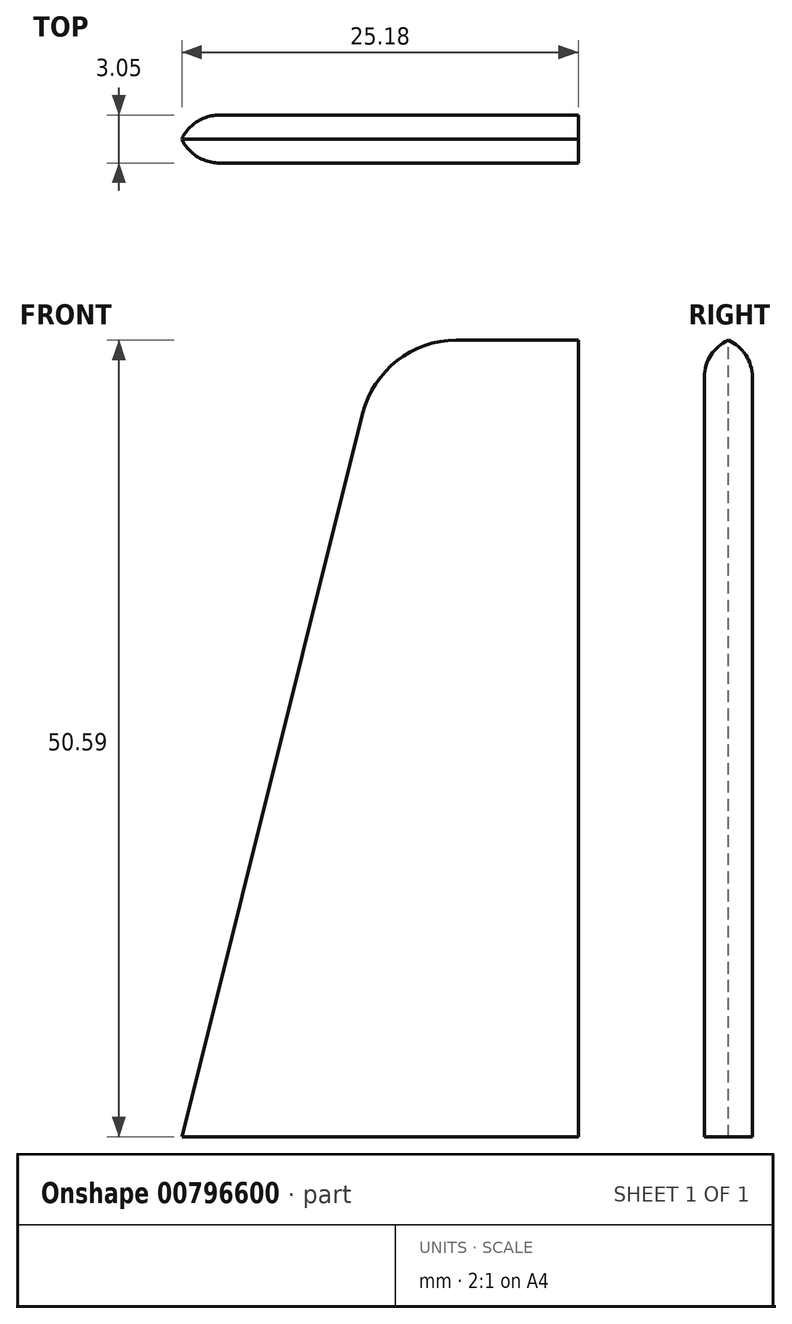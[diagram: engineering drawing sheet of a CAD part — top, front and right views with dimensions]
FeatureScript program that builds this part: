
annotation { "Feature Type Name" : "Feature", "Feature Type Description" : "" }
export const myFeature = defineFeature(function(context is Context, id is Id, definition is map)
    precondition{}
    {
        {
            var Q0;
            Q0=qCreatedBy(makeId("Front.planeOp"),FACE);
            var sketch = newSketch(context, id + "F0", { "sketchPlane" : qUnion([Q0])});
            skLineSegment(sketch, "E0", {"start": v(17.66, 50.8) * mm, "end": v(25.4, 50.8) * mm});
            skLineSegment(sketch, "E1", {"start": v(25.4, 50.8) * mm, "end": v(25.4, 0) * mm});
            skLineSegment(sketch, "E2", {"start": v(25.4, 0) * mm, "end": v(0, 0) * mm});
            skLineSegment(sketch, "E3", {"start": v(0, 0) * mm, "end": v(11.5, 46) * mm});
            skPoint(sketch, "E4.visualSharp", {"position": v(12.7, 50.8) * mm});
            skArc(sketch, "E4.filletArc", {"start": v(17.66, 50.8) * mm, "mid": v(13.75, 49.46) * mm, "end": v(11.5, 46) * mm});
            skSolve(sketch);
        }
        {
            var Q0;
            Q0=makeQuery(id+"F0.imprint","IMPRINT",FACE,{"disambiguationData":[TD([[makeQuery(id+"F0.imprint","IMPRINT",EDGE,{"derivedFrom":sQuery(id+"F0.wireOp",EDGE,"E0")}),-1.0]])]});
            extrude(context, id + "F1", {"entities" : qUnion([Q0]), "depth" : 3.05 * mm, "offsetDistance" : 25.4 * mm});
        }
        {
            var Q0;
            Q0=makeQuery(id+"F1.opExtrude","CAP_EDGE",EDGE,{"disambiguationData":[OSD([sQuery(id+"F0.wireOp",EDGE,"E3")])],"isStart":false});
            var Q1;
            Q1=makeQuery(id+"F1.opExtrude","CAP_EDGE",EDGE,{"disambiguationData":[OSD([sQuery(id+"F0.wireOp",EDGE,"E3")])],"isStart":true});
            fillet(context, id + "F2", {"entities" : qUnion([Q0, Q1]), "radius" : 2.54 * mm, "tangentPropagation" : true, "allowEdgeOverflow" : false});
        }
    });
